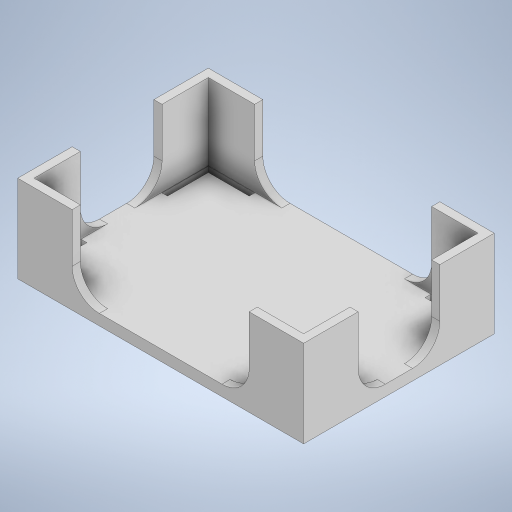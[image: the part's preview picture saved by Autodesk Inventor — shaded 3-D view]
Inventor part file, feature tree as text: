
AUTODESK INVENTOR PART (.ipt)
format: ipt  version: 2024.2 (Build 282272000, 272)  size: 326,144 bytes
history: native  units: mm
features: extrude x3, sketch x3, fillet x1
ambient origin geometry x8: Origin, YZ Plane, XZ Plane, XY Plane, X Axis, Y Axis, Z Axis, Center Point
bodies: Solid1 (feature_tree)
feature tree (7):
  extrude  "Extrusion1"  Depth=70.0mm
  extrude  "Extrusion2"  Depth=17.0mm
  extrude  "Extrusion3"  Depth=17.0mm
  fillet  "Fillet2"  Radius=2.0mm
  sketch  "Sketch1"  dims[d0=105.0mm d1=70.0mm]
  sketch  "Sketch2"  dims[d2=4.0mm d3=0.0mm d4=17.0mm]
  sketch  "Sketch3"  dims[d5=2.0mm d6=17.0mm d7=2.0mm d8=3.2mm d9=3.2mm d10=52.5mm d11=35.0mm d12=6.0mm d13=0.0mm d15=20.0mm d16=3.0mm d17=20.0mm d18=3.0mm d19=52.5mm d20=35.0mm d21=28.0mm d22=0.0mm d23=10.0mm]
